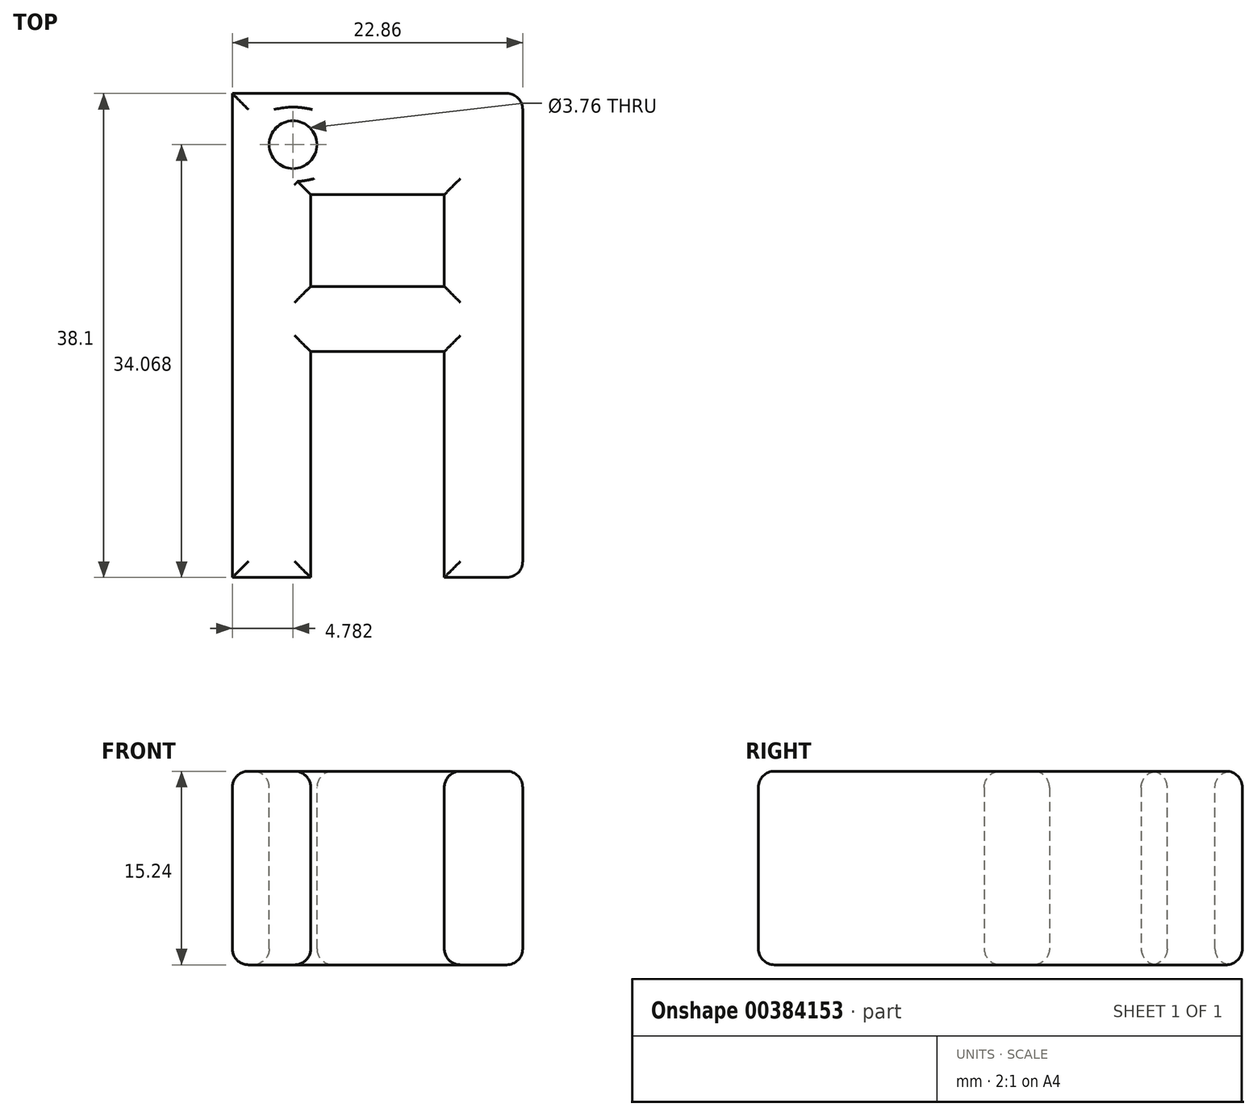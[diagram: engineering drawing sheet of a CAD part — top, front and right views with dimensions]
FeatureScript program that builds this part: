
annotation { "Feature Type Name" : "Feature", "Feature Type Description" : "" }
export const myFeature = defineFeature(function(context is Context, id is Id, definition is map)
    precondition{}
    {
        {
            var Q0;
            Q0=qCreatedBy(makeId("Top.planeOp"),FACE);
            var sketch = newSketch(context, id + "F0", { "sketchPlane" : qUnion([Q0])});
            skLineSegment(sketch, "E0", {"start": v(-36.21, 0) * mm, "end": v(-36.21, 38.1) * mm});
            skLineSegment(sketch, "E1", {"start": v(-36.21, 38.1) * mm, "end": v(-13.35, 38.1) * mm});
            skLineSegment(sketch, "E2", {"start": v(-13.35, 38.1) * mm, "end": v(-13.35, 0) * mm});
            skLineSegment(sketch, "E3", {"start": v(-19.52, 0) * mm, "end": v(-13.35, 0) * mm});
            skLineSegment(sketch, "E4", {"start": v(-36.21, 0) * mm, "end": v(-30.04, 0) * mm});
            skLineSegment(sketch, "E5", {"start": v(-30.04, 0) * mm, "end": v(-30.04, 17.78) * mm});
            skLineSegment(sketch, "E6", {"start": v(-19.52, 0) * mm, "end": v(-19.52, 17.78) * mm});
            skLineSegment(sketch, "E7", {"start": v(-30.04, 17.78) * mm, "end": v(-19.52, 17.78) * mm});
            skLineSegment(sketch, "E8", {"start": v(-30.04, 22.91) * mm, "end": v(-19.52, 22.91) * mm});
            skLineSegment(sketch, "E9", {"start": v(-19.52, 22.91) * mm, "end": v(-19.52, 30.14) * mm});
            skLineSegment(sketch, "E10", {"start": v(-19.52, 30.14) * mm, "end": v(-30.04, 30.14) * mm});
            skLineSegment(sketch, "E11", {"start": v(-30.04, 30.14) * mm, "end": v(-30.04, 22.91) * mm});
            skSolve(sketch);
        }
        {
            var Q0;
            Q0 = qSketchRegion(id + "F0", true);
            extrude(context, id + "F1", {"entities" : qUnion([Q0]), "depth" : 15.24 * mm});
        }
        {
            var Q0;
            Q0=makeQuery(id+"F1.opExtrude","CAP_FACE",FACE,{"disambiguationData":[OSD([sQuery(id+"F0.wireOp",EDGE,"E0"),sQuery(id+"F0.wireOp",EDGE,"E1"),sQuery(id+"F0.wireOp",EDGE,"E2"),sQuery(id+"F0.wireOp",EDGE,"E3"),sQuery(id+"F0.wireOp",EDGE,"E4"),sQuery(id+"F0.wireOp",EDGE,"E5"),sQuery(id+"F0.wireOp",EDGE,"E6"),sQuery(id+"F0.wireOp",EDGE,"E7"),sQuery(id+"F0.wireOp",EDGE,"E8"),sQuery(id+"F0.wireOp",EDGE,"E9"),sQuery(id+"F0.wireOp",EDGE,"E10"),sQuery(id+"F0.wireOp",EDGE,"E11")])],"isStart":false});
            var sketch = newSketch(context, id + "F2", { "sketchPlane" : qUnion([Q0])});
            skCircle(sketch, "E12", {"center": v(-31.43, 34.07) * mm, "radius": 1.88 * mm});
            skSolve(sketch);
        }
        {
            var Q0;
            Q0 = qSketchRegion(id + "F2", true);
            extrude(context, id + "F3", {"entities" : qUnion([Q0]), "operationType" : NewBodyOperationType.REMOVE, "oppositeDirection" : true, "depth" : 25.4 * mm});
        }
        {
            var Q0;
            Q0=makeQuery(id+"F1.opExtrude","CAP_FACE",FACE,{"disambiguationData":[OSD([sQuery(id+"F0.wireOp",EDGE,"E0"),sQuery(id+"F0.wireOp",EDGE,"E1"),sQuery(id+"F0.wireOp",EDGE,"E2"),sQuery(id+"F0.wireOp",EDGE,"E3"),sQuery(id+"F0.wireOp",EDGE,"E4"),sQuery(id+"F0.wireOp",EDGE,"E5"),sQuery(id+"F0.wireOp",EDGE,"E6"),sQuery(id+"F0.wireOp",EDGE,"E7"),sQuery(id+"F0.wireOp",EDGE,"E8"),sQuery(id+"F0.wireOp",EDGE,"E9"),sQuery(id+"F0.wireOp",EDGE,"E10"),sQuery(id+"F0.wireOp",EDGE,"E11")])],"isStart":false});
            var Q1;
            Q1=makeQuery(id+"F1.opExtrude","CAP_FACE",FACE,{"disambiguationData":[OSD([sQuery(id+"F0.wireOp",EDGE,"E0"),sQuery(id+"F0.wireOp",EDGE,"E1"),sQuery(id+"F0.wireOp",EDGE,"E2"),sQuery(id+"F0.wireOp",EDGE,"E3"),sQuery(id+"F0.wireOp",EDGE,"E4"),sQuery(id+"F0.wireOp",EDGE,"E5"),sQuery(id+"F0.wireOp",EDGE,"E6"),sQuery(id+"F0.wireOp",EDGE,"E7"),sQuery(id+"F0.wireOp",EDGE,"E8"),sQuery(id+"F0.wireOp",EDGE,"E9"),sQuery(id+"F0.wireOp",EDGE,"E10"),sQuery(id+"F0.wireOp",EDGE,"E11")])],"isStart":true});
            var Q2;
            Q2=makeQuery(id+"F1.opExtrude","SWEPT_FACE",FACE,{"disambiguationData":[OSD([sQuery(id+"F0.wireOp",EDGE,"E2")])]});
            fillet(context, id + "F4", {"entities" : qUnion([Q0, Q1, Q2]), "radius" : 1.27 * mm, "tangentPropagation" : true, "allowEdgeOverflow" : false});
        }
    });
